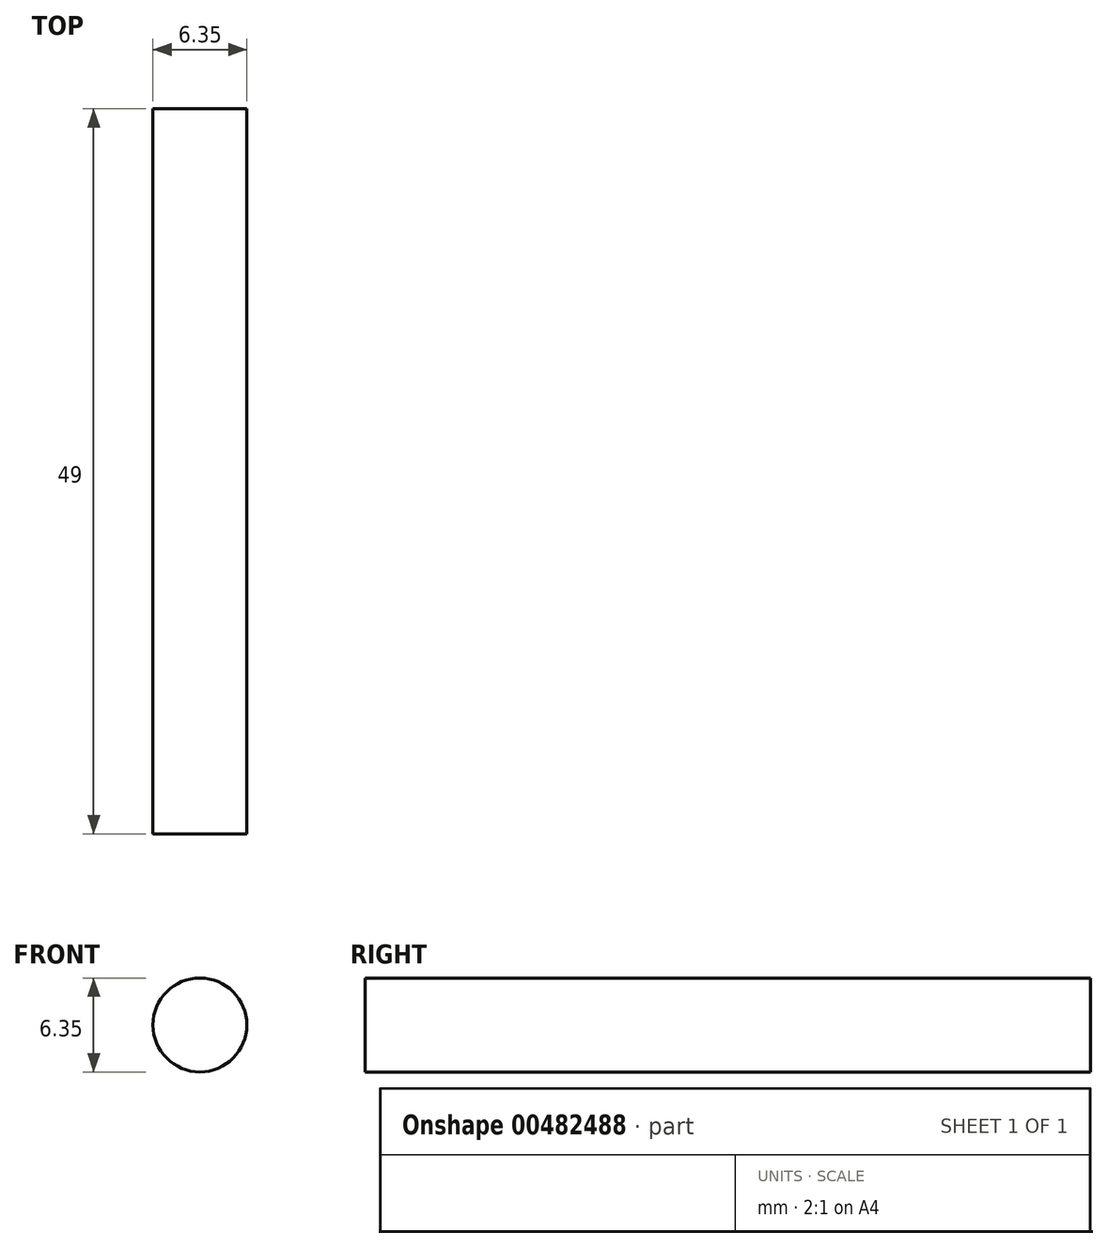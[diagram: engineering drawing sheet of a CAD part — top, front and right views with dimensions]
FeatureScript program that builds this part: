
annotation { "Feature Type Name" : "Feature", "Feature Type Description" : "" }
export const myFeature = defineFeature(function(context is Context, id is Id, definition is map)
    precondition{}
    {
        {
            var Q0;
            Q0=qCreatedBy(makeId("Front.planeOp"),FACE);
            var sketch = newSketch(context, id + "F0", { "sketchPlane" : qUnion([Q0])});
            skCircle(sketch, "E0", {"center": v(-55.73, 23.26) * mm, "radius": 3.18 * mm});
            skSolve(sketch);
        }
        {
            var Q0;
            Q0=makeQuery(id+"F0.imprint","IMPRINT",FACE,{"disambiguationData":[TD([[makeQuery(id+"F0.imprint","IMPRINT",EDGE,{"derivedFrom":sQuery(id+"F0.wireOp",EDGE,"E0")}),1.0]])]});
            extrude(context, id + "F1", {"entities" : qUnion([Q0]), "depth" : 49 * mm, "offsetDistance" : 25 * mm});
        }
    });
